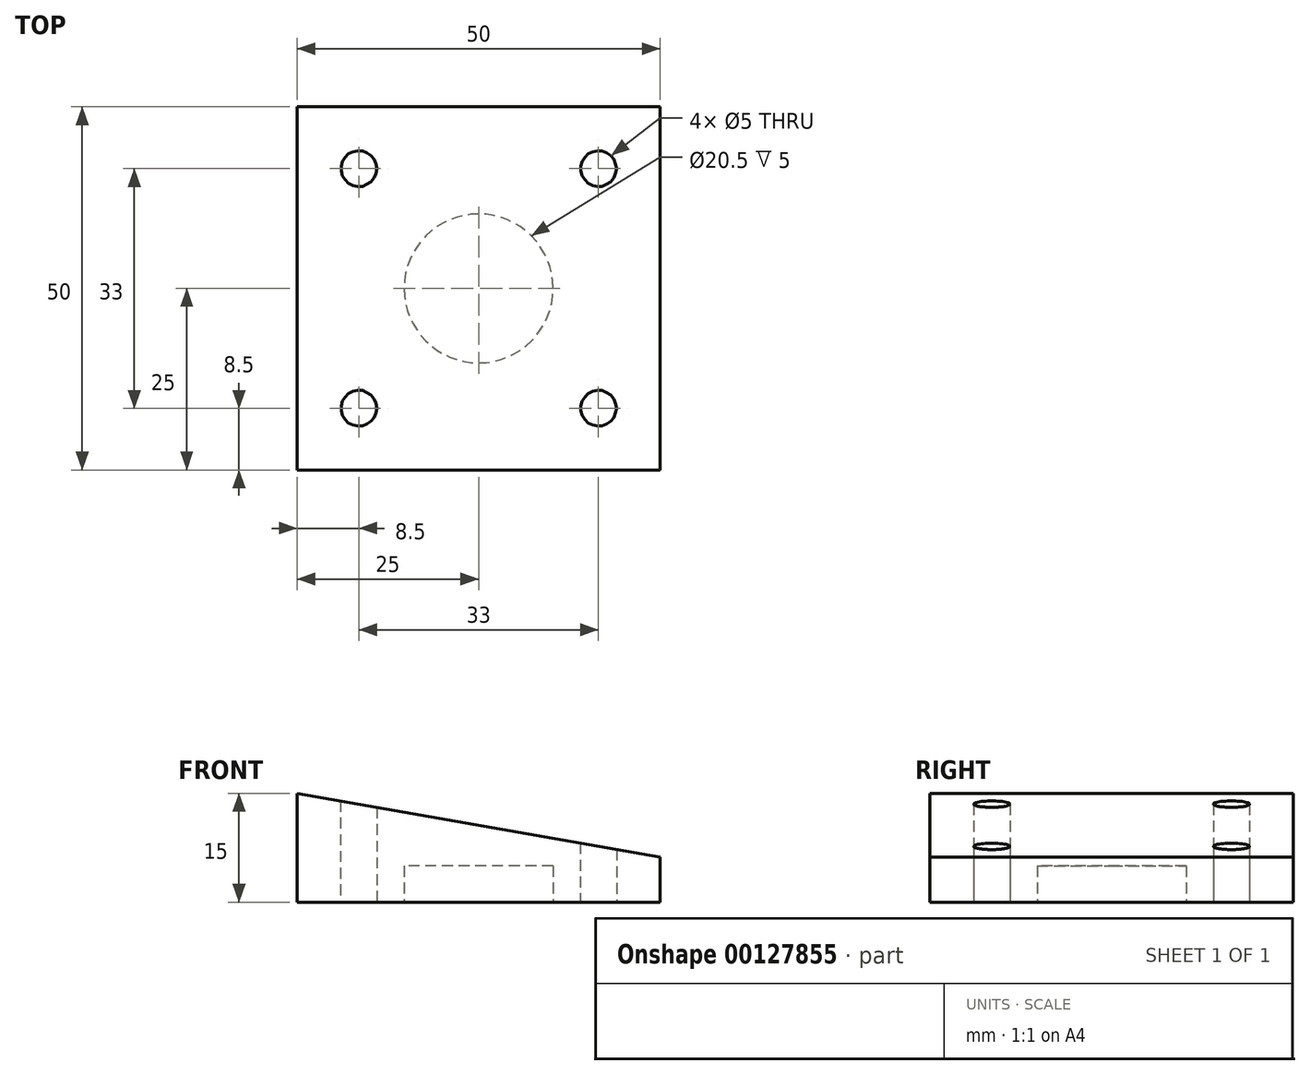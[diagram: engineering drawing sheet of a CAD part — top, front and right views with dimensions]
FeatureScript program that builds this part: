
annotation { "Feature Type Name" : "Feature", "Feature Type Description" : "" }
export const myFeature = defineFeature(function(context is Context, id is Id, definition is map)
    precondition{}
    {
        {
            var Q0;
            Q0=qCreatedBy(makeId("Top.planeOp"),FACE);
            var sketch = newSketch(context, id + "F0", { "sketchPlane" : qUnion([Q0])});
            skLineSegment(sketch, "E0.bottom", {"start": v(25, 25) * mm, "end": v(-25, 25) * mm});
            skLineSegment(sketch, "E0.top", {"start": v(25, -25) * mm, "end": v(-25, -25) * mm});
            skLineSegment(sketch, "E0.left", {"start": v(25, 25) * mm, "end": v(25, -25) * mm});
            skLineSegment(sketch, "E0.right", {"start": v(-25, 25) * mm, "end": v(-25, -25) * mm});
            skPoint(sketch, "E0.middle", {"position": v(0, 0) * mm});
            skCircle(sketch, "E1", {"center": v(0, 0) * mm, "radius": 9.55 * mm});
            skLineSegment(sketch, "E2", {"start": v(0, 43.44) * mm, "end": v(0, -47.36) * mm, "construction": true});
            skPoint(sketch, "E2.endSnap0", {"position": v(0, 25) * mm});
            skLineSegment(sketch, "E3", {"start": v(-43.35, 0) * mm, "end": v(44.28, 0) * mm, "construction": true});
            skCircle(sketch, "E4", {"center": v(-16.5, 16.5) * mm, "radius": 2.5 * mm});
            skCircle(sketch, "E5.MirrorC", {"center": v(16.5, 16.5) * mm, "radius": 2.5 * mm});
            skCircle(sketch, "E6.MirrorC", {"center": v(-16.5, -16.5) * mm, "radius": 2.5 * mm});
            skCircle(sketch, "E7.MirrorC", {"center": v(16.5, -16.5) * mm, "radius": 2.5 * mm});
            skSolve(sketch);
        }
        {
            var Q0;
            Q0=makeQuery(id+"F0.imprint","IMPRINT",FACE,{"disambiguationData":[TD([[makeQuery(id+"F0.imprint","IMPRINT",EDGE,{"derivedFrom":sQuery(id+"F0.wireOp",EDGE,"E0.bottom")}),1.0]])]});
            var Q1;
            Q1=makeQuery(id+"F0.imprint","IMPRINT",FACE,{"disambiguationData":[TD([[makeQuery(id+"F0.imprint","IMPRINT",EDGE,{"derivedFrom":sQuery(id+"F0.wireOp",EDGE,"E1")}),1.0]])]});
            extrude(context, id + "F1", {"entities" : qUnion([Q0, Q1]), "depth" : 15 * mm});
        }
        {
            var Q0;
            Q0=qCreatedBy(makeId("Front.planeOp"),FACE);
            var sketch = newSketch(context, id + "F2", { "sketchPlane" : qUnion([Q0])});
            skLineSegment(sketch, "E8", {"start": v(-25, 15) * mm, "end": v(25, 15) * mm});
            skLineSegment(sketch, "E9", {"start": v(25, 15) * mm, "end": v(25, 6.18) * mm});
            skLineSegment(sketch, "E10", {"start": v(25, 6.18) * mm, "end": v(-25, 15) * mm});
            skLineSegment(sketch, "E11.0.1", {"start": v(25, 15) * mm, "end": v(-25, 15) * mm});
            skSolve(sketch);
        }
        {
            var Q0;
            Q0 = qSketchRegion(id + "F2", true);
            extrude(context, id + "F3", {"entities" : qUnion([Q0]), "operationType" : NewBodyOperationType.REMOVE, "endBound" : BoundingType.SYMMETRIC, "oppositeDirection" : true, "depth" : 50 * mm});
        }
        {
            var Q0;
            Q0=qCreatedBy(makeId("Top.planeOp"),FACE);
            var sketch = newSketch(context, id + "F4", { "sketchPlane" : qUnion([Q0])});
            skCircle(sketch, "E12", {"center": v(0, 0) * mm, "radius": 10.25 * mm});
            skSolve(sketch);
        }
        {
            var Q0;
            Q0 = qSketchRegion(id + "F4", true);
            extrude(context, id + "F5", {"entities" : qUnion([Q0]), "operationType" : NewBodyOperationType.REMOVE, "depth" : 5 * mm});
        }
    });
